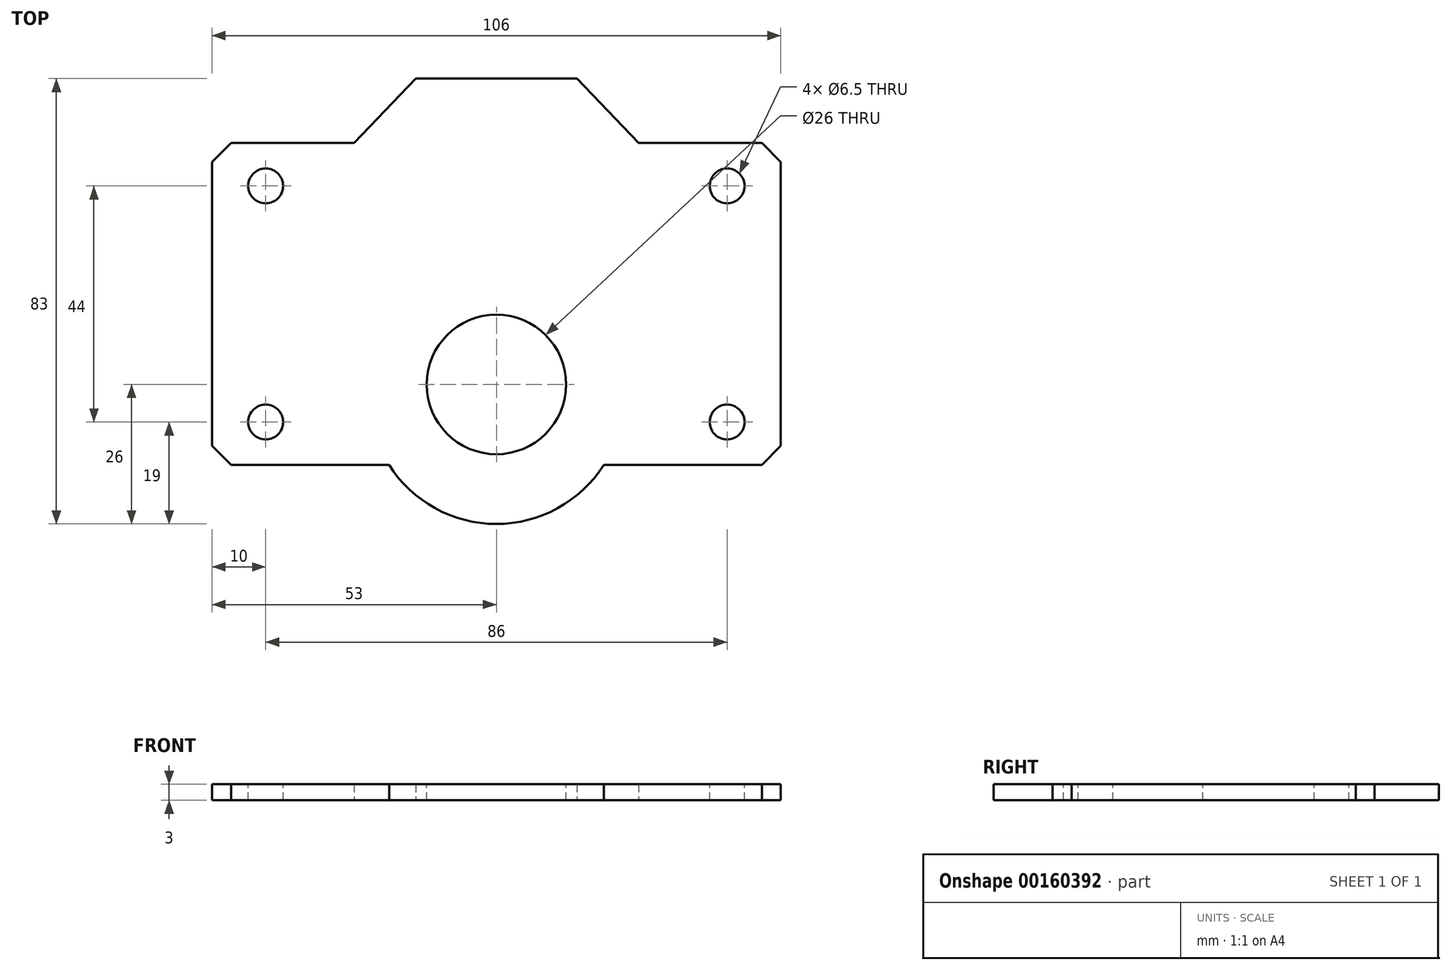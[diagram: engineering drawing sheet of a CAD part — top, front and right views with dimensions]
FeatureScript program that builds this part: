
annotation { "Feature Type Name" : "Feature", "Feature Type Description" : "" }
export const myFeature = defineFeature(function(context is Context, id is Id, definition is map)
    precondition{}
    {
        {
            var Q0;
            Q0=qCreatedBy(makeId("Top.planeOp"),FACE);
            var sketch = newSketch(context, id + "F0", { "sketchPlane" : qUnion([Q0])});
            skLineSegment(sketch, "E0.bottom", {"start": v(-49.46, 30) * mm, "end": v(-26.5, 30) * mm});
            skLineSegment(sketch, "E0.top", {"start": v(-49.46, -30) * mm, "end": v(-20, -30) * mm});
            skLineSegment(sketch, "E0.left", {"start": v(-53, 26.46) * mm, "end": v(-53, -26.46) * mm});
            skLineSegment(sketch, "E0.right", {"start": v(53, 26.46) * mm, "end": v(53, -26.46) * mm});
            skPoint(sketch, "E0.middle", {"position": v(0, 0) * mm});
            skLineSegment(sketch, "E1", {"start": v(-26.5, 30) * mm, "end": v(-15, 42) * mm});
            skLineSegment(sketch, "E2", {"start": v(-15, 42) * mm, "end": v(15, 42) * mm});
            skLineSegment(sketch, "E3", {"start": v(15, 42) * mm, "end": v(26.5, 30) * mm});
            skLineSegment(sketch, "E4", {"start": v(0, 42) * mm, "end": v(0, 0) * mm, "construction": true});
            skLineSegment(sketch, "E5.trimOffspring", {"start": v(26.5, 30) * mm, "end": v(49.46, 30) * mm});
            skArc(sketch, "E6", {"start": v(-20, -30) * mm, "mid": v(0, -41) * mm, "end": v(20, -30) * mm});
            skLineSegment(sketch, "E7.trimOffspring", {"start": v(20, -30) * mm, "end": v(49.46, -30) * mm});
            skLineSegment(sketch, "E8", {"start": v(-20, -30) * mm, "end": v(20, -30) * mm, "construction": true});
            skLineSegment(sketch, "E9.0", {"start": v(-58, 28.54) * mm, "end": v(-58, -28.54) * mm, "construction": true});
            skLineSegment(sketch, "E9.1", {"start": v(-51.54, -35) * mm, "end": v(-22.58, -35) * mm, "construction": true});
            skLineSegment(sketch, "E9.2", {"start": v(-51.54, 35) * mm, "end": v(-28.63, 35) * mm, "construction": true});
            skArc(sketch, "E9.3", {"start": v(-22.58, -35) * mm, "mid": v(0, -46) * mm, "end": v(22.58, -35) * mm, "construction": true});
            skLineSegment(sketch, "E9.4", {"start": v(22.58, -35) * mm, "end": v(51.54, -35) * mm, "construction": true});
            skLineSegment(sketch, "E9.5", {"start": v(58, 28.54) * mm, "end": v(58, -28.54) * mm, "construction": true});
            skLineSegment(sketch, "E9.6", {"start": v(-28.63, 35) * mm, "end": v(-17.13, 47) * mm, "construction": true});
            skLineSegment(sketch, "E9.7", {"start": v(-17.13, 47) * mm, "end": v(17.13, 47) * mm, "construction": true});
            skLineSegment(sketch, "E9.8", {"start": v(17.13, 47) * mm, "end": v(28.63, 35) * mm, "construction": true});
            skLineSegment(sketch, "E9.9", {"start": v(28.63, 35) * mm, "end": v(51.54, 35) * mm, "construction": true});
            skLineSegment(sketch, "E10", {"start": v(-49.46, 30) * mm, "end": v(-53, 26.46) * mm});
            skLineSegment(sketch, "E11", {"start": v(-53, -26.46) * mm, "end": v(-49.46, -30) * mm});
            skLineSegment(sketch, "E12", {"start": v(49.46, -30) * mm, "end": v(53, -26.46) * mm});
            skLineSegment(sketch, "E13", {"start": v(49.46, 30) * mm, "end": v(53, 26.46) * mm});
            skLineSegment(sketch, "E14.0", {"start": v(-51.54, 35) * mm, "end": v(-58, 28.54) * mm, "construction": true});
            skLineSegment(sketch, "E15.0", {"start": v(51.54, 35) * mm, "end": v(58, 28.54) * mm, "construction": true});
            skLineSegment(sketch, "E16.0", {"start": v(51.54, -35) * mm, "end": v(58, -28.54) * mm, "construction": true});
            skLineSegment(sketch, "E17.0", {"start": v(-58, -28.54) * mm, "end": v(-51.54, -35) * mm, "construction": true});
            skPoint(sketch, "E18.orphan", {"position": v(-53, -30) * mm});
            skPoint(sketch, "E19.orphan", {"position": v(-53, 30) * mm});
            skPoint(sketch, "E20.orphan", {"position": v(53, 30) * mm});
            skPoint(sketch, "E21.orphan", {"position": v(53, -30) * mm});
            skSolve(sketch);
        }
        {
            var Q0;
            Q0 = qSketchRegion(id + "F0", true);
            extrude(context, id + "F1", {"entities" : qUnion([Q0]), "depth" : 3 * mm});
        }
        {
            var Q0;
            Q0=makeQuery(id+"F1.opExtrude","CAP_FACE",FACE,{"disambiguationData":[OSD([sQuery(id+"F0.wireOp",EDGE,"E0.bottom"),sQuery(id+"F0.wireOp",EDGE,"E0.top"),sQuery(id+"F0.wireOp",EDGE,"E0.left"),sQuery(id+"F0.wireOp",EDGE,"E0.right"),sQuery(id+"F0.wireOp",EDGE,"E1"),sQuery(id+"F0.wireOp",EDGE,"E2"),sQuery(id+"F0.wireOp",EDGE,"E3"),sQuery(id+"F0.wireOp",EDGE,"E5.trimOffspring"),sQuery(id+"F0.wireOp",EDGE,"E6"),sQuery(id+"F0.wireOp",EDGE,"E7.trimOffspring"),sQuery(id+"F0.wireOp",EDGE,"E10"),sQuery(id+"F0.wireOp",EDGE,"E11"),sQuery(id+"F0.wireOp",EDGE,"E12"),sQuery(id+"F0.wireOp",EDGE,"E13")])],"isStart":false});
            var sketch = newSketch(context, id + "F2", { "sketchPlane" : qUnion([Q0])});
            skCircle(sketch, "E22", {"center": v(0, -15) * mm, "radius": 13 * mm});
            skPoint(sketch, "E23.start.orphan", {"position": v(0, -28) * mm});
            skSolve(sketch);
        }
        {
            var Q0;
            Q0 = qSketchRegion(id + "F2", true);
            extrude(context, id + "F3", {"entities" : qUnion([Q0]), "operationType" : NewBodyOperationType.REMOVE, "endBound" : BoundingType.THROUGH_ALL, "oppositeDirection" : true, "depth" : 25 * mm});
        }
        {
            var Q0;
            Q0=makeQuery(id+"F2.imprint","IMPRINT",FACE,{"disambiguationData":[TD([[makeQuery(id+"F2.imprint","IMPRINT",EDGE,{"derivedFrom":sQuery(id+"F2.wireOp",EDGE,"E22")}),-1.0]])]});
            var sketch = newSketch(context, id + "F4", { "sketchPlane" : qUnion([Q0])});
            skCircle(sketch, "E24", {"center": v(-43, 22) * mm, "radius": 3.25 * mm});
            skCircle(sketch, "E25", {"center": v(-43, -22) * mm, "radius": 3.25 * mm});
            skCircle(sketch, "E26", {"center": v(43, 22) * mm, "radius": 3.25 * mm});
            skCircle(sketch, "E27", {"center": v(43, -22) * mm, "radius": 3.25 * mm});
            skSolve(sketch);
        }
        {
            var Q0;
            Q0 = qSketchRegion(id + "F4", true);
            extrude(context, id + "F5", {"entities" : qUnion([Q0]), "operationType" : NewBodyOperationType.REMOVE, "endBound" : BoundingType.THROUGH_ALL, "oppositeDirection" : true, "depth" : 25 * mm});
        }
    });
